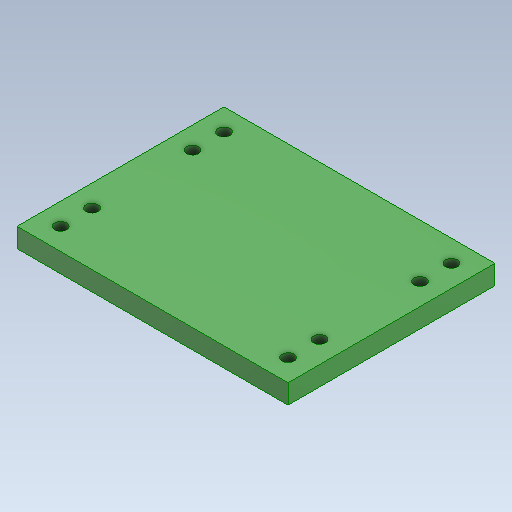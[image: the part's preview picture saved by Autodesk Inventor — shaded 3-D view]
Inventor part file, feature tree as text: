
AUTODESK INVENTOR PART (.ipt)
format: ipt  version: 2020 (Build 240168000, 168)  size: 97,280 bytes
history: native  units: in
note: dims shown in document units (in); Inventor stores cm internally (conversion verified against a paired STEP export)
features: mirror x1
ambient origin geometry x8: Origin, YZ Plane, XZ Plane, XY Plane, X Axis, Y Axis, Z Axis, Center Point
bodies: Solid1 (feature_tree)
feature tree (1):
  mirror  "Mirror2"
